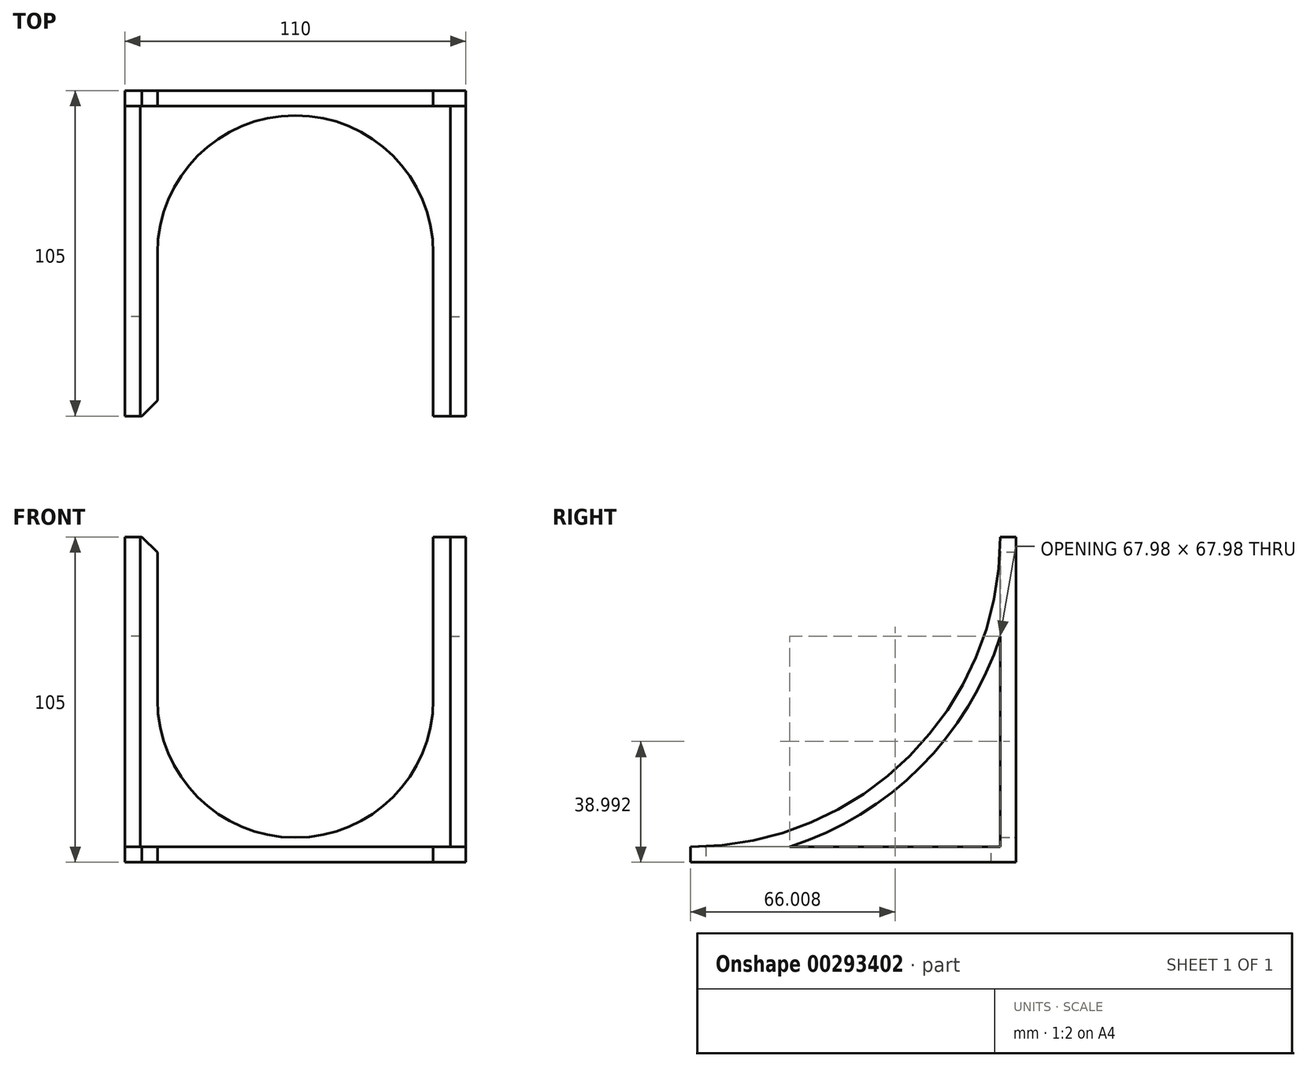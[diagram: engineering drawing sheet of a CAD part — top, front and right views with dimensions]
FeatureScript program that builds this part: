
annotation { "Feature Type Name" : "Feature", "Feature Type Description" : "" }
export const myFeature = defineFeature(function(context is Context, id is Id, definition is map)
    precondition{}
    {
        {
            var Q0;
            Q0=qCreatedBy(makeId("Top.planeOp"),FACE);
            var sketch = newSketch(context, id + "F0", { "sketchPlane" : qUnion([Q0])});
            skLineSegment(sketch, "E0.bottom", {"start": v(55, 52.5) * mm, "end": v(-55, 52.5) * mm});
            skLineSegment(sketch, "E0.top", {"start": v(55, -52.5) * mm, "end": v(-55, -52.5) * mm});
            skLineSegment(sketch, "E0.left", {"start": v(55, 52.5) * mm, "end": v(55, -52.5) * mm});
            skLineSegment(sketch, "E0.right", {"start": v(-55, 52.5) * mm, "end": v(-55, -52.5) * mm});
            skPoint(sketch, "E0.middle", {"position": v(0, 0) * mm});
            skSolve(sketch);
        }
        {
            var Q0;
            Q0=makeQuery(id+"F0.imprint","IMPRINT",FACE,{"disambiguationData":[TD([[makeQuery(id+"F0.imprint","IMPRINT",EDGE,{"derivedFrom":sQuery(id+"F0.wireOp",EDGE,"E0.bottom")}),1.0]])]});
            extrude(context, id + "F1", {"entities" : qUnion([Q0]), "depth" : 5 * mm});
        }
        {
            var Q0;
            Q0=makeQuery(id+"F1.opExtrude","CAP_FACE",FACE,{"disambiguationData":[OSD([sQuery(id+"F0.wireOp",EDGE,"E0.bottom"),sQuery(id+"F0.wireOp",EDGE,"E0.top"),sQuery(id+"F0.wireOp",EDGE,"E0.left"),sQuery(id+"F0.wireOp",EDGE,"E0.right")])],"isStart":false});
            var sketch = newSketch(context, id + "F2", { "sketchPlane" : qUnion([Q0])});
            skLineSegment(sketch, "E1.bottom", {"start": v(-55, 52.5) * mm, "end": v(55, 52.5) * mm});
            skLineSegment(sketch, "E1.top", {"start": v(-55, 47.5) * mm, "end": v(55, 47.5) * mm});
            skLineSegment(sketch, "E1.left", {"start": v(-55, 52.5) * mm, "end": v(-55, 47.5) * mm});
            skLineSegment(sketch, "E1.right", {"start": v(55, 52.5) * mm, "end": v(55, 47.5) * mm});
            skSolve(sketch);
        }
        {
            var Q0;
            Q0=makeQuery(id+"F2.imprint","IMPRINT",FACE,{"disambiguationData":[TD([[makeQuery(id+"F2.imprint","IMPRINT",EDGE,{"derivedFrom":sQuery(id+"F2.wireOp",EDGE,"E1.bottom")}),1.0]])]});
            extrude(context, id + "F3", {"entities" : qUnion([Q0]), "operationType" : NewBodyOperationType.ADD, "depth" : 100 * mm});
        }
        {
            var Q0;
            Q0=makeQuery(id+"F3.boolean.opBoolean","MERGE",FACE,{"derivedFrom":[makeQuery(id+"F1.opExtrude","SWEPT_FACE",FACE,{"disambiguationData":[OSD([sQuery(id+"F0.wireOp",EDGE,"E0.right")])]}),makeQuery(id+"F3.opExtrude","SWEPT_FACE",FACE,{"disambiguationData":[OSD([sQuery(id+"F2.wireOp",EDGE,"E1.left")])]})]});
            var sketch = newSketch(context, id + "F4", { "sketchPlane" : qUnion([Q0])});
            skArc(sketch, "E2", {"start": v(-47.5, 105) * mm, "mid": v(-18.21, 34.29) * mm, "end": v(52.5, 5) * mm});
            skArc(sketch, "E3", {"start": v(-52.5, 105) * mm, "mid": v(-21.75, 30.75) * mm, "end": v(52.5, 0) * mm});
            skLineSegment(sketch, "E4", {"start": v(-52.5, 105) * mm, "end": v(-47.5, 105) * mm});
            skLineSegment(sketch, "E5", {"start": v(52.5, 5) * mm, "end": v(52.5, 0) * mm});
            skSolve(sketch);
        }
        {
            var Q0;
            {var subQ0=sQuery(id+"F4.wireOp",EDGE,"E2");Q0=makeQuery(id+"F4.imprint","IMPRINT",FACE,{"disambiguationData":[TD([[makeQuery(id+"F4.imprint","IMPRINT",EDGE,{"derivedFrom":subQ0}),-1.0]])]});}
            extrude(context, id + "F5", {"entities" : qUnion([Q0]), "operationType" : NewBodyOperationType.ADD, "oppositeDirection" : true, "depth" : 5 * mm});
        }
        {
            var Q0;
            Q0=makeQuery(id+"F1.opExtrude","SWEPT_BODY",BODY,{"disambiguationData":[OSD([sQuery(id+"F0.wireOp",EDGE,"E0.bottom"),sQuery(id+"F0.wireOp",EDGE,"E0.top"),sQuery(id+"F0.wireOp",EDGE,"E0.left"),sQuery(id+"F0.wireOp",EDGE,"E0.right")])]});
            var Q1;
            Q1=qCreatedBy(makeId("Right.planeOp"),FACE);
            mirror(context, id + "F6", {"operationType" : NewBodyOperationType.ADD, "entities" : qUnion([Q0]), "mirrorPlane" : qUnion([Q1])});
        }
        {
            var Q0;
            Q0=makeQuery(id+"F1.opExtrude","CAP_FACE",FACE,{"disambiguationData":[OSD([sQuery(id+"F0.wireOp",EDGE,"E0.bottom"),sQuery(id+"F0.wireOp",EDGE,"E0.top"),sQuery(id+"F0.wireOp",EDGE,"E0.left"),sQuery(id+"F0.wireOp",EDGE,"E0.right")])],"isStart":false});
            var sketch = newSketch(context, id + "F7", { "sketchPlane" : qUnion([Q0])});
            skArc(sketch, "E6", {"start": v(44.5, 0) * mm, "mid": v(0, 44.5) * mm, "end": v(-44.5, 0) * mm});
            skLineSegment(sketch, "E7", {"start": v(-44.5, 0) * mm, "end": v(-44.5, -52.5) * mm});
            skLineSegment(sketch, "E8", {"start": v(44.5, 0) * mm, "end": v(44.5, -52.5) * mm});
            skLineSegment(sketch, "E9", {"start": v(44.5, -52.5) * mm, "end": v(-44.5, -52.5) * mm});
            skSolve(sketch);
        }
        {
            var Q0;
            Q0=makeQuery(id+"F7.imprint","IMPRINT",FACE,{"disambiguationData":[TD([[makeQuery(id+"F7.imprint","IMPRINT",EDGE,{"derivedFrom":sQuery(id+"F7.wireOp",EDGE,"E6")}),1.0]])]});
            extrude(context, id + "F8", {"entities" : qUnion([Q0]), "operationType" : NewBodyOperationType.REMOVE, "endBound" : BoundingType.THROUGH_ALL, "oppositeDirection" : true, "depth" : 25 * mm});
        }
        {
            var Q0;
            Q0=makeQuery(id+"F3.boolean.opBoolean","MERGE",FACE,{"derivedFrom":[makeQuery(id+"F1.opExtrude","SWEPT_FACE",FACE,{"disambiguationData":[OSD([sQuery(id+"F0.wireOp",EDGE,"E0.bottom")])]}),makeQuery(id+"F3.opExtrude","SWEPT_FACE",FACE,{"disambiguationData":[OSD([sQuery(id+"F2.wireOp",EDGE,"E1.bottom")])]})]});
            var sketch = newSketch(context, id + "F9", { "sketchPlane" : qUnion([Q0])});
            skLineSegment(sketch, "E10", {"start": v(-55, 52.5) * mm, "end": v(0, 52.5) * mm, "construction": true});
            skLineSegment(sketch, "E11", {"start": v(0, 52.5) * mm, "end": v(0, 0) * mm, "construction": true});
            skArc(sketch, "E12", {"start": v(-44.5, 52.5) * mm, "mid": v(0, 8) * mm, "end": v(44.5, 52.5) * mm});
            skLineSegment(sketch, "E13", {"start": v(-44.5, 52.5) * mm, "end": v(-44.5, 105) * mm});
            skLineSegment(sketch, "E14", {"start": v(44.5, 52.5) * mm, "end": v(44.5, 105) * mm});
            skLineSegment(sketch, "E15", {"start": v(44.5, 105) * mm, "end": v(-44.5, 105) * mm});
            skSolve(sketch);
        }
        {
            var Q0;
            Q0 = qSketchRegion(id + "F9", true);
            extrude(context, id + "F10", {"entities" : qUnion([Q0]), "operationType" : NewBodyOperationType.REMOVE, "endBound" : BoundingType.THROUGH_ALL, "oppositeDirection" : true, "depth" : 25 * mm});
        }
        {
            var Q0;
            Q0=makeQuery(id+"F10.boolean.opBoolean","COPY",EDGE,{"derivedFrom":makeQuery(id+"F10.opExtrude","SWEPT_EDGE",EDGE,{"disambiguationData":[OSD([sQuery(id+"F2.wireOp",EDGE,"E1.bottom"),sQuery(id+"F9.wireOp",EDGE,"E13"),sQuery(id+"F9.wireOp",EDGE,"E15")])]})});
            var Q1;
            Q1=makeQuery(id+"F10.boolean.opBoolean","COPY",EDGE,{"derivedFrom":makeQuery(id+"F10.opExtrude","SWEPT_EDGE",EDGE,{"disambiguationData":[OSD([sQuery(id+"F2.wireOp",EDGE,"E1.bottom"),sQuery(id+"F9.wireOp",EDGE,"E14"),sQuery(id+"F9.wireOp",EDGE,"E15")])]})});
            var Q2;
            Q2=makeQuery(id+"F8.boolean.opBoolean","COPY",EDGE,{"derivedFrom":makeQuery(id+"F8.opExtrude","SWEPT_EDGE",EDGE,{"disambiguationData":[OSD([sQuery(id+"F0.wireOp",EDGE,"E0.top"),sQuery(id+"F7.wireOp",EDGE,"E8"),sQuery(id+"F7.wireOp",EDGE,"E9")])]})});
            var Q3;
            Q3=makeQuery(id+"F8.boolean.opBoolean","COPY",EDGE,{"derivedFrom":makeQuery(id+"F8.opExtrude","SWEPT_EDGE",EDGE,{"disambiguationData":[OSD([sQuery(id+"F0.wireOp",EDGE,"E0.top"),sQuery(id+"F7.wireOp",EDGE,"E7"),sQuery(id+"F7.wireOp",EDGE,"E9")])]})});
            chamfer(context, id + "F11", {"entities" : qUnion([Q0, Q1, Q2, Q3]), "width" : 5 * mm, "tangentPropagation" : true});
        }
    });
